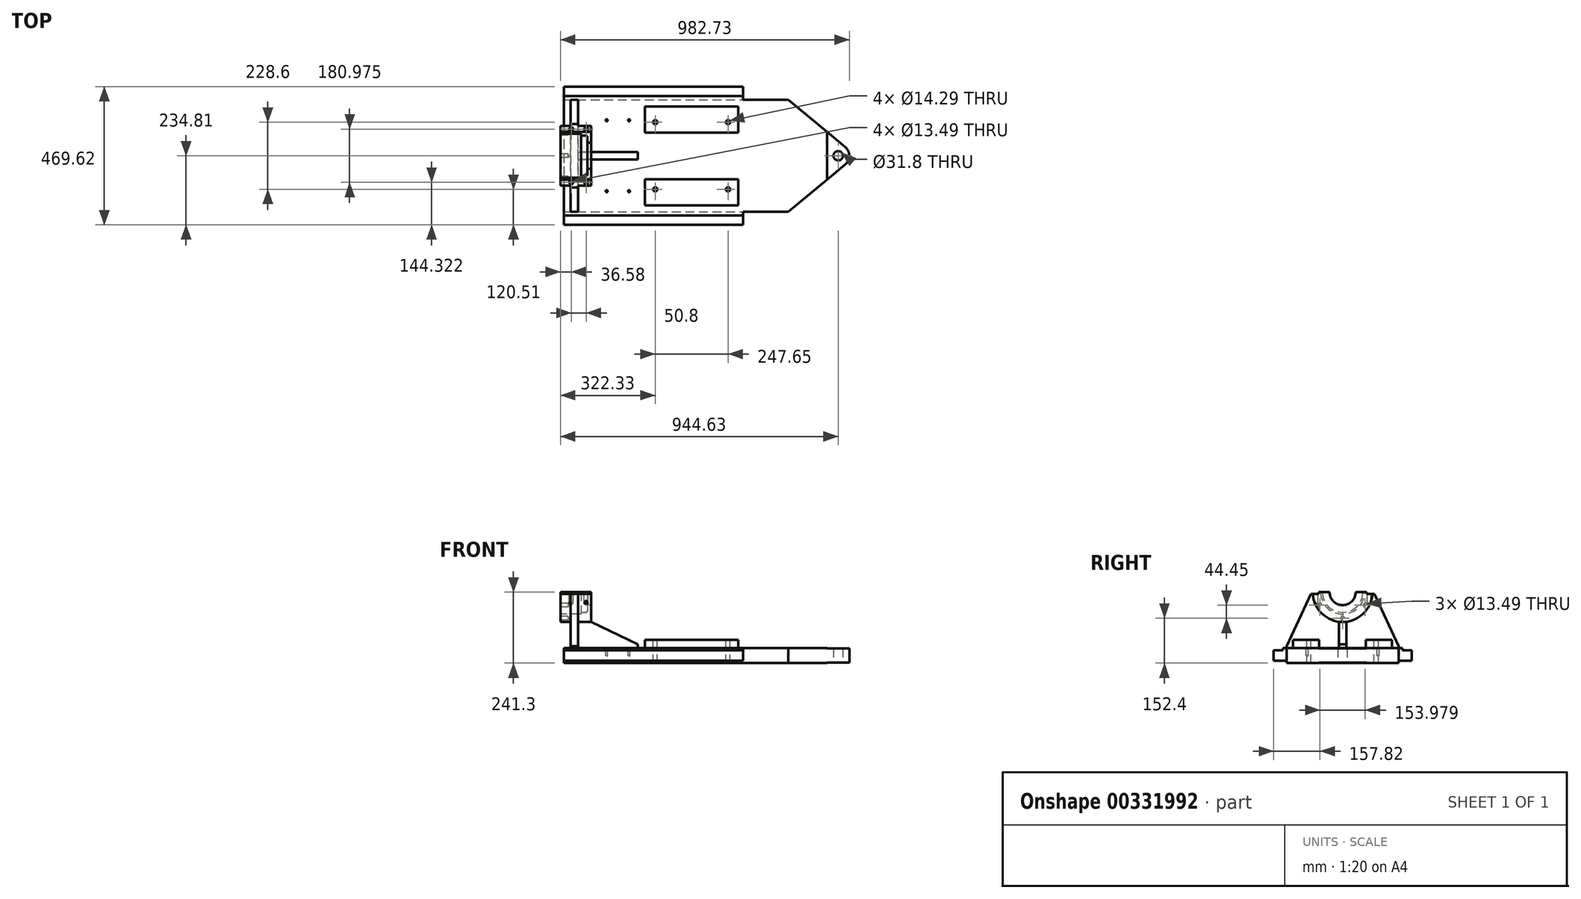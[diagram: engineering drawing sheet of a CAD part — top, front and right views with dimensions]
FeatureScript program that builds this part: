
annotation { "Feature Type Name" : "Feature", "Feature Type Description" : "" }
export const myFeature = defineFeature(function(context is Context, id is Id, definition is map)
    precondition{}
    {
        {
            var Q0;
            Q0=qCreatedBy(makeId("Top.planeOp"),FACE);
            var sketch = newSketch(context, id + "F0", { "sketchPlane" : qUnion([Q0])});
            skLineSegment(sketch, "E0.bottom", {"start": v(-304.8, 234.81) * mm, "end": v(304.8, 234.81) * mm});
            skLineSegment(sketch, "E0.top", {"start": v(-304.8, -234.81) * mm, "end": v(304.8, -234.81) * mm});
            skLineSegment(sketch, "E0.left", {"start": v(-304.8, 234.81) * mm, "end": v(-304.8, -234.81) * mm});
            skPoint(sketch, "E0.middle", {"position": v(0, 0) * mm});
            skLineSegment(sketch, "E1.0", {"start": v(666.75, 234.81) * mm, "end": v(666.75, -234.81) * mm, "construction": true});
            skLineSegment(sketch, "E2.0", {"start": v(628.65, 234.81) * mm, "end": v(628.65, -234.81) * mm, "construction": true});
            skLineSegment(sketch, "E3", {"start": v(459.57, 190.5) * mm, "end": v(653.04, 29.27) * mm});
            skLineSegment(sketch, "E4", {"start": v(459.57, -190.5) * mm, "end": v(656.3, -26.56) * mm});
            skLineSegment(sketch, "E5", {"start": v(304.8, 234.81) * mm, "end": v(304.8, 190.5) * mm});
            skLineSegment(sketch, "E6", {"start": v(-414.48, 0) * mm, "end": v(838.18, 0) * mm, "construction": true});
            skArc(sketch, "E7", {"start": v(653.04, -29.27) * mm, "mid": v(666.75, 0) * mm, "end": v(653.04, 29.27) * mm});
            skCircle(sketch, "E8", {"center": v(628.65, 0) * mm, "radius": 15.9 * mm});
            skLineSegment(sketch, "E9.0", {"start": v(-414.48, -190.5) * mm, "end": v(-304.8, -190.5) * mm});
            skLineSegment(sketch, "E10.trimOffspring", {"start": v(304.8, -190.5) * mm, "end": v(459.57, -190.5) * mm});
            skPoint(sketch, "E11.top.end.orphan", {"position": v(406.4, -234.81) * mm});
            skLineSegment(sketch, "E12.trimOffspring", {"start": v(628.65, -190.5) * mm, "end": v(838.18, -190.5) * mm});
            skLineSegment(sketch, "E13.MirrorCS", {"start": v(304.8, 190.5) * mm, "end": v(459.57, 190.5) * mm});
            skLineSegment(sketch, "E14.trimOffspring", {"start": v(304.8, -190.5) * mm, "end": v(304.8, -234.81) * mm});
            skSolve(sketch);
        }
        {
            var Q0;
            Q0 = qSketchRegion(id + "F0", true);
            extrude(context, id + "F1", {"entities" : qUnion([Q0]), "endBound" : BoundingType.SYMMETRIC, "depth" : 50.8 * mm});
        }
        {
            var Q0;
            Q0=makeQuery(id+"F1.opExtrude","CAP_FACE",FACE,{"disambiguationData":[OSD([sQuery(id+"F0.wireOp",EDGE,"E0.bottom"),sQuery(id+"F0.wireOp",EDGE,"E0.top"),sQuery(id+"F0.wireOp",EDGE,"E0.left"),sQuery(id+"F0.wireOp",EDGE,"E3"),sQuery(id+"F0.wireOp",EDGE,"E4"),sQuery(id+"F0.wireOp",EDGE,"E5"),sQuery(id+"F0.wireOp",EDGE,"E7"),sQuery(id+"F0.wireOp",EDGE,"E8"),sQuery(id+"F0.wireOp",EDGE,"E10.trimOffspring"),sQuery(id+"F0.wireOp",EDGE,"E13.MirrorCS"),sQuery(id+"F0.wireOp",EDGE,"E14.trimOffspring")])],"isStart":false});
            var sketch = newSketch(context, id + "F2", { "sketchPlane" : qUnion([Q0])});
            skCircle(sketch, "E15.0", {"center": v(628.65, 0) * mm, "radius": 15.9 * mm, "construction": true});
            skLineSegment(sketch, "E16.bottom", {"start": v(590.55, 101.6) * mm, "end": v(666.75, 101.6) * mm});
            skLineSegment(sketch, "E16.top", {"start": v(590.55, -101.6) * mm, "end": v(666.75, -101.6) * mm});
            skLineSegment(sketch, "E16.left", {"start": v(590.55, 101.6) * mm, "end": v(590.55, -101.6) * mm});
            skLineSegment(sketch, "E16.right", {"start": v(666.75, 101.6) * mm, "end": v(666.75, -101.6) * mm});
            skSolve(sketch);
        }
        {
            var Q0;
            Q0 = qSketchRegion(id + "F2", true);
            extrude(context, id + "F3", {"entities" : qUnion([Q0]), "operationType" : NewBodyOperationType.REMOVE, "oppositeDirection" : true, "depth" : 1.59 * mm});
        }
        {
            var Q0;
            Q0=makeQuery(id+"F1.opExtrude","CAP_FACE",FACE,{"disambiguationData":[OSD([sQuery(id+"F0.wireOp",EDGE,"E0.bottom"),sQuery(id+"F0.wireOp",EDGE,"E0.top"),sQuery(id+"F0.wireOp",EDGE,"E0.left"),sQuery(id+"F0.wireOp",EDGE,"E3"),sQuery(id+"F0.wireOp",EDGE,"E4"),sQuery(id+"F0.wireOp",EDGE,"E5"),sQuery(id+"F0.wireOp",EDGE,"E7"),sQuery(id+"F0.wireOp",EDGE,"E8"),sQuery(id+"F0.wireOp",EDGE,"E10.trimOffspring"),sQuery(id+"F0.wireOp",EDGE,"E13.MirrorCS"),sQuery(id+"F0.wireOp",EDGE,"E14.trimOffspring")])],"isStart":true});
            var sketch = newSketch(context, id + "F4", { "sketchPlane" : qUnion([Q0])});
            skCircle(sketch, "E17.0", {"center": v(628.65, 0) * mm, "radius": 15.9 * mm, "construction": true});
            skLineSegment(sketch, "E18.bottom", {"start": v(590.55, 101.6) * mm, "end": v(666.75, 101.6) * mm});
            skLineSegment(sketch, "E18.top", {"start": v(590.55, -101.6) * mm, "end": v(666.75, -101.6) * mm});
            skLineSegment(sketch, "E18.left", {"start": v(590.55, 101.6) * mm, "end": v(590.55, -101.6) * mm});
            skLineSegment(sketch, "E18.right", {"start": v(666.75, 101.6) * mm, "end": v(666.75, -101.6) * mm});
            skSolve(sketch);
        }
        {
            var Q0;
            Q0 = qSketchRegion(id + "F4", true);
            extrude(context, id + "F5", {"entities" : qUnion([Q0]), "operationType" : NewBodyOperationType.REMOVE, "oppositeDirection" : true, "depth" : 1.59 * mm});
        }
        {
            var Q0;
            Q0=makeQuery(id+"F1.opExtrude","CAP_FACE",FACE,{"disambiguationData":[OSD([sQuery(id+"F0.wireOp",EDGE,"E0.bottom"),sQuery(id+"F0.wireOp",EDGE,"E0.top"),sQuery(id+"F0.wireOp",EDGE,"E0.left"),sQuery(id+"F0.wireOp",EDGE,"E3"),sQuery(id+"F0.wireOp",EDGE,"E4"),sQuery(id+"F0.wireOp",EDGE,"E5"),sQuery(id+"F0.wireOp",EDGE,"E7"),sQuery(id+"F0.wireOp",EDGE,"E8"),sQuery(id+"F0.wireOp",EDGE,"E10.trimOffspring"),sQuery(id+"F0.wireOp",EDGE,"E13.MirrorCS"),sQuery(id+"F0.wireOp",EDGE,"E14.trimOffspring")])],"isStart":false});
            var sketch = newSketch(context, id + "F6", { "sketchPlane" : qUnion([Q0])});
            skLineSegment(sketch, "E19", {"start": v(-362.8, 0) * mm, "end": v(684.09, 0) * mm, "construction": true});
            skLineSegment(sketch, "E20.0", {"start": v(-362.8, -203.2) * mm, "end": v(684.09, -203.2) * mm, "construction": true});
            skLineSegment(sketch, "E21.0", {"start": v(-304.8, 234.81) * mm, "end": v(-304.8, -234.81) * mm, "construction": true});
            skLineSegment(sketch, "E22.0", {"start": v(304.8, -190.5) * mm, "end": v(304.8, -234.81) * mm, "construction": true});
            skLineSegment(sketch, "E23.bottom", {"start": v(-304.8, -234.81) * mm, "end": v(332.24, -234.81) * mm});
            skLineSegment(sketch, "E23.top", {"start": v(-304.8, -203.2) * mm, "end": v(332.24, -203.2) * mm});
            skLineSegment(sketch, "E23.left", {"start": v(-304.8, -234.81) * mm, "end": v(-304.8, -203.2) * mm});
            skLineSegment(sketch, "E23.right", {"start": v(332.24, -234.81) * mm, "end": v(332.24, -203.2) * mm});
            skLineSegment(sketch, "E24.MirrorCS", {"start": v(332.24, 234.81) * mm, "end": v(332.24, 203.2) * mm});
            skLineSegment(sketch, "E25.MirrorCS", {"start": v(-304.8, 234.81) * mm, "end": v(-304.8, 203.2) * mm});
            skLineSegment(sketch, "E26.MirrorCS", {"start": v(-304.8, 203.2) * mm, "end": v(332.24, 203.2) * mm});
            skLineSegment(sketch, "E27.MirrorCS", {"start": v(-304.8, 234.81) * mm, "end": v(332.24, 234.81) * mm});
            skLineSegment(sketch, "E28.MirrorCS", {"start": v(304.8, 190.5) * mm, "end": v(304.8, 234.81) * mm, "construction": true});
            skSolve(sketch);
        }
        {
            var Q0;
            Q0 = qSketchRegion(id + "F6", true);
            extrude(context, id + "F7", {"entities" : qUnion([Q0]), "operationType" : NewBodyOperationType.REMOVE, "oppositeDirection" : true, "depth" : 7.94 * mm});
        }
        {
            var Q0;
            Q0=makeQuery(id+"F1.opExtrude","CAP_FACE",FACE,{"disambiguationData":[OSD([sQuery(id+"F0.wireOp",EDGE,"E0.bottom"),sQuery(id+"F0.wireOp",EDGE,"E0.top"),sQuery(id+"F0.wireOp",EDGE,"E0.left"),sQuery(id+"F0.wireOp",EDGE,"E3"),sQuery(id+"F0.wireOp",EDGE,"E4"),sQuery(id+"F0.wireOp",EDGE,"E5"),sQuery(id+"F0.wireOp",EDGE,"E7"),sQuery(id+"F0.wireOp",EDGE,"E8"),sQuery(id+"F0.wireOp",EDGE,"E10.trimOffspring"),sQuery(id+"F0.wireOp",EDGE,"E13.MirrorCS"),sQuery(id+"F0.wireOp",EDGE,"E14.trimOffspring")])],"isStart":true});
            var sketch = newSketch(context, id + "F8", { "sketchPlane" : qUnion([Q0])});
            skLineSegment(sketch, "E29", {"start": v(-400.34, 0) * mm, "end": v(753.76, 0) * mm, "construction": true});
            skLineSegment(sketch, "E30.0", {"start": v(-304.8, -234.81) * mm, "end": v(-304.8, 234.81) * mm, "construction": true});
            skLineSegment(sketch, "E31.0", {"start": v(-400.34, -190.5) * mm, "end": v(753.76, -190.5) * mm, "construction": true});
            skLineSegment(sketch, "E32.bottom", {"start": v(-304.8, -190.5) * mm, "end": v(475.01, -190.5) * mm});
            skLineSegment(sketch, "E32.top", {"start": v(-304.8, -283.73) * mm, "end": v(475.01, -283.73) * mm});
            skLineSegment(sketch, "E32.left", {"start": v(-304.8, -190.5) * mm, "end": v(-304.8, -283.73) * mm});
            skLineSegment(sketch, "E32.right", {"start": v(475.01, -190.5) * mm, "end": v(475.01, -283.73) * mm});
            skLineSegment(sketch, "E33.MirrorCS", {"start": v(475.01, 190.5) * mm, "end": v(475.01, 283.73) * mm});
            skLineSegment(sketch, "E34.MirrorCS", {"start": v(-304.8, 190.5) * mm, "end": v(-304.8, 283.73) * mm});
            skLineSegment(sketch, "E35.MirrorCS", {"start": v(-304.8, 283.73) * mm, "end": v(475.01, 283.73) * mm});
            skLineSegment(sketch, "E36.MirrorCS", {"start": v(-304.8, 190.5) * mm, "end": v(475.01, 190.5) * mm});
            skSolve(sketch);
        }
        {
            var Q0;
            Q0 = qSketchRegion(id + "F8", true);
            extrude(context, id + "F9", {"entities" : qUnion([Q0]), "operationType" : NewBodyOperationType.REMOVE, "oppositeDirection" : true, "depth" : 7.94 * mm});
        }
        {
            var Q0;
            Q0=makeQuery(id+"F1.opExtrude","CAP_FACE",FACE,{"disambiguationData":[OSD([sQuery(id+"F0.wireOp",EDGE,"E0.bottom"),sQuery(id+"F0.wireOp",EDGE,"E0.top"),sQuery(id+"F0.wireOp",EDGE,"E0.left"),sQuery(id+"F0.wireOp",EDGE,"E3"),sQuery(id+"F0.wireOp",EDGE,"E4"),sQuery(id+"F0.wireOp",EDGE,"E5"),sQuery(id+"F0.wireOp",EDGE,"E7"),sQuery(id+"F0.wireOp",EDGE,"E8"),sQuery(id+"F0.wireOp",EDGE,"E10.trimOffspring"),sQuery(id+"F0.wireOp",EDGE,"E13.MirrorCS"),sQuery(id+"F0.wireOp",EDGE,"E14.trimOffspring")])],"isStart":false});
            var sketch = newSketch(context, id + "F10", { "sketchPlane" : qUnion([Q0])});
            skLineSegment(sketch, "E37", {"start": v(-417.52, 0) * mm, "end": v(724.3, 0) * mm, "construction": true});
            skLineSegment(sketch, "E38.0", {"start": v(-304.8, 203.2) * mm, "end": v(-304.8, -203.2) * mm, "construction": true});
            skLineSegment(sketch, "E39.0", {"start": v(-28.57, 203.2) * mm, "end": v(-28.57, -203.2) * mm, "construction": true});
            skLineSegment(sketch, "E40.0", {"start": v(288.93, 203.2) * mm, "end": v(288.93, -203.2) * mm, "construction": true});
            skLineSegment(sketch, "E41.0", {"start": v(-417.52, -79.38) * mm, "end": v(724.3, -79.38) * mm, "construction": true});
            skLineSegment(sketch, "E42.bottom", {"start": v(-28.57, -79.38) * mm, "end": v(288.93, -79.38) * mm});
            skLineSegment(sketch, "E42.top", {"start": v(-28.57, -168.28) * mm, "end": v(288.93, -168.28) * mm});
            skLineSegment(sketch, "E42.left", {"start": v(-28.57, -79.38) * mm, "end": v(-28.57, -168.28) * mm});
            skLineSegment(sketch, "E42.right", {"start": v(288.93, -79.38) * mm, "end": v(288.93, -168.28) * mm});
            skLineSegment(sketch, "E43.MirrorCS", {"start": v(-28.57, 168.28) * mm, "end": v(288.93, 168.28) * mm});
            skLineSegment(sketch, "E44.MirrorCS", {"start": v(288.93, 79.38) * mm, "end": v(288.93, 168.28) * mm});
            skLineSegment(sketch, "E45.MirrorCS", {"start": v(-28.57, 79.38) * mm, "end": v(-28.57, 168.28) * mm});
            skLineSegment(sketch, "E46.MirrorCS", {"start": v(-28.57, 79.38) * mm, "end": v(288.93, 79.38) * mm});
            skSolve(sketch);
        }
        {
            var Q0;
            Q0 = qSketchRegion(id + "F10", true);
            extrude(context, id + "F11", {"entities" : qUnion([Q0]), "operationType" : NewBodyOperationType.ADD, "depth" : 28.57 * mm});
        }
        {
            var Q0;
            Q0=makeQuery(id+"F11.opExtrude","CAP_FACE",FACE,{"disambiguationData":[OSD([sQuery(id+"F10.wireOp",EDGE,"E43.MirrorCS"),sQuery(id+"F10.wireOp",EDGE,"E44.MirrorCS"),sQuery(id+"F10.wireOp",EDGE,"E45.MirrorCS"),sQuery(id+"F10.wireOp",EDGE,"E46.MirrorCS")])],"isStart":false});
            var sketch = newSketch(context, id + "F12", { "sketchPlane" : qUnion([Q0])});
            skCircle(sketch, "E47.0", {"center": v(628.65, 0) * mm, "radius": 15.9 * mm, "construction": true});
            skLineSegment(sketch, "E48", {"start": v(628.65, 0) * mm, "end": v(628.65, 304) * mm, "construction": true});
            skLineSegment(sketch, "E49", {"start": v(-454.06, 0) * mm, "end": v(702.68, 0) * mm, "construction": true});
            skLineSegment(sketch, "E50.0", {"start": v(-454.06, 114.3) * mm, "end": v(702.68, 114.3) * mm, "construction": true});
            skLineSegment(sketch, "E51.0", {"start": v(254, 0) * mm, "end": v(254, 304) * mm, "construction": true});
            skLineSegment(sketch, "E52.0", {"start": v(6.35, 0) * mm, "end": v(6.35, 304) * mm, "construction": true});
            skPoint(sketch, "E53", {"position": v(6.35, 114.3) * mm});
            skPoint(sketch, "E54", {"position": v(254, 114.3) * mm});
            skPoint(sketch, "E55.MirrorP", {"position": v(254, -114.3) * mm});
            skPoint(sketch, "E56.MirrorP", {"position": v(6.35, -114.3) * mm});
            skSolve(sketch);
        }
        {
            var Q0;
            Q0=sQuery(id+"F12.wireOp",VERTEX,"E53");
            var Q1;
            Q1=sQuery(id+"F12.wireOp",VERTEX,"E54");
            var Q2;
            Q2=sQuery(id+"F12.wireOp",VERTEX,"E56.MirrorP");
            var Q3;
            Q3=sQuery(id+"F12.wireOp",VERTEX,"E55.MirrorP");
            var Q4;
            Q4=makeQuery(id+"F1.opExtrude","SWEPT_BODY",BODY,{"disambiguationData":[OSD([sQuery(id+"F0.wireOp",EDGE,"E0.bottom"),sQuery(id+"F0.wireOp",EDGE,"E0.top"),sQuery(id+"F0.wireOp",EDGE,"E0.left"),sQuery(id+"F0.wireOp",EDGE,"E3"),sQuery(id+"F0.wireOp",EDGE,"E4"),sQuery(id+"F0.wireOp",EDGE,"E5"),sQuery(id+"F0.wireOp",EDGE,"E7"),sQuery(id+"F0.wireOp",EDGE,"E8"),sQuery(id+"F0.wireOp",EDGE,"E10.trimOffspring"),sQuery(id+"F0.wireOp",EDGE,"E13.MirrorCS"),sQuery(id+"F0.wireOp",EDGE,"E14.trimOffspring")])]});
            hole(context, id + "F13", {"style" : HoleStyle.SIMPLE, "endStyle" : HoleEndStyle.THROUGH, "holeDiameter" : 14.29 * mm, "tappedDepth" : 19.53 * mm, "tapClearance" : 3, "locations" : qUnion([Q0, Q1, Q2, Q3]), "scope" : qUnion([Q4])});
        }
        {
            var Q0;
            Q0=makeQuery(id+"F1.opExtrude","CAP_FACE",FACE,{"disambiguationData":[OSD([sQuery(id+"F0.wireOp",EDGE,"E0.bottom"),sQuery(id+"F0.wireOp",EDGE,"E0.top"),sQuery(id+"F0.wireOp",EDGE,"E0.left"),sQuery(id+"F0.wireOp",EDGE,"E3"),sQuery(id+"F0.wireOp",EDGE,"E4"),sQuery(id+"F0.wireOp",EDGE,"E5"),sQuery(id+"F0.wireOp",EDGE,"E7"),sQuery(id+"F0.wireOp",EDGE,"E8"),sQuery(id+"F0.wireOp",EDGE,"E10.trimOffspring"),sQuery(id+"F0.wireOp",EDGE,"E13.MirrorCS"),sQuery(id+"F0.wireOp",EDGE,"E14.trimOffspring")])],"isStart":false});
            var sketch = newSketch(context, id + "F14", { "sketchPlane" : qUnion([Q0])});
            skLineSegment(sketch, "E57.0", {"start": v(-304.8, 203.2) * mm, "end": v(-304.8, -203.2) * mm, "construction": true});
            skLineSegment(sketch, "E58.0", {"start": v(-280.99, 203.2) * mm, "end": v(-280.99, -203.2) * mm, "construction": true});
            skLineSegment(sketch, "E59", {"start": v(-408.3, 0) * mm, "end": v(198.31, 0) * mm, "construction": true});
            skLineSegment(sketch, "E60.0", {"start": v(-408.3, -190.5) * mm, "end": v(198.31, -190.5) * mm, "construction": true});
            skLineSegment(sketch, "E61.bottom", {"start": v(-280.99, -190.5) * mm, "end": v(-255.59, -190.5) * mm});
            skLineSegment(sketch, "E61.top", {"start": v(-280.99, 190.5) * mm, "end": v(-255.59, 190.5) * mm});
            skLineSegment(sketch, "E61.left", {"start": v(-280.99, -190.5) * mm, "end": v(-280.99, 190.5) * mm});
            skLineSegment(sketch, "E61.right", {"start": v(-255.59, -190.5) * mm, "end": v(-255.59, 190.5) * mm});
            skSolve(sketch);
        }
        {
            var Q0;
            Q0 = qSketchRegion(id + "F14", true);
            extrude(context, id + "F15", {"entities" : qUnion([Q0]), "operationType" : NewBodyOperationType.ADD, "depth" : 190.5 * mm});
        }
        {
            var Q0;
            Q0=makeQuery(id+"F1.opExtrude","SWEPT_FACE",FACE,{"disambiguationData":[OSD([sQuery(id+"F0.wireOp",EDGE,"E0.left")])]});
            cPlane(context, id + "F16", {"entities" : qUnion([Q0]), "cplaneType" : CPlaneType.OFFSET, "offset" : 11.18 * mm, "width" : 152.4 * mm, "height" : 152.4 * mm});
        }
        {
            var Q0;
            Q0=qCreatedBy(id+"F16.planeOp",FACE);
            var sketch = newSketch(context, id + "F17", { "sketchPlane" : qUnion([Q0])});
            skLineSegment(sketch, "E62.0", {"start": v(190.5, 215.9) * mm, "end": v(-190.5, 215.9) * mm, "construction": true});
            skLineSegment(sketch, "E63", {"start": v(0, 334.76) * mm, "end": v(0, -159.92) * mm, "construction": true});
            skCircle(sketch, "E64", {"center": v(0, 215.9) * mm, "radius": 101.6 * mm});
            skSolve(sketch);
        }
        {
            var Q0;
            Q0 = qSketchRegion(id + "F17", true);
            extrude(context, id + "F18", {"entities" : qUnion([Q0]), "operationType" : NewBodyOperationType.ADD, "oppositeDirection" : true, "depth" : 104.77 * mm});
        }
        {
            var Q0;
            Q0=makeQuery(id+"F15.opExtrude","SWEPT_FACE",FACE,{"disambiguationData":[OSD([sQuery(id+"F14.wireOp",EDGE,"E61.left")])]});
            var sketch = newSketch(context, id + "F19", { "sketchPlane" : qUnion([Q0])});
            skCircle(sketch, "E65.0", {"center": v(0, 215.9) * mm, "radius": 101.6 * mm, "construction": true});
            skLineSegment(sketch, "E66.0", {"start": v(-203.2, 31.75) * mm, "end": v(203.2, 31.75) * mm, "construction": true});
            skLineSegment(sketch, "E67.0", {"start": v(-190.5, 215.9) * mm, "end": v(-190.5, 25.4) * mm, "construction": true});
            skLineSegment(sketch, "E68", {"start": v(-190.5, 31.75) * mm, "end": v(-107.95, 209.55) * mm});
            skLineSegment(sketch, "E69", {"start": v(-107.95, 209.55) * mm, "end": v(-80.96, 209.55) * mm});
            skLineSegment(sketch, "E70", {"start": v(-80.96, 209.55) * mm, "end": v(-80.96, 215.9) * mm});
            skLineSegment(sketch, "E71", {"start": v(-80.96, 215.9) * mm, "end": v(0, 215.9) * mm});
            skLineSegment(sketch, "E72", {"start": v(0, 356.38) * mm, "end": v(0, -105.82) * mm, "construction": true});
            skLineSegment(sketch, "E73.MirrorCS", {"start": v(80.96, 209.55) * mm, "end": v(80.96, 215.9) * mm});
            skLineSegment(sketch, "E74.MirrorCS", {"start": v(80.96, 215.9) * mm, "end": v(0, 215.9) * mm});
            skLineSegment(sketch, "E75.MirrorCS", {"start": v(190.5, 31.75) * mm, "end": v(107.95, 209.55) * mm});
            skLineSegment(sketch, "E76.MirrorCS", {"start": v(190.5, 215.9) * mm, "end": v(190.5, 25.4) * mm, "construction": true});
            skLineSegment(sketch, "E77.MirrorCS", {"start": v(107.95, 209.55) * mm, "end": v(80.96, 209.55) * mm});
            skLineSegment(sketch, "E78", {"start": v(-190.5, 31.75) * mm, "end": v(-190.5, 348.54) * mm});
            skLineSegment(sketch, "E79", {"start": v(-190.5, 348.54) * mm, "end": v(190.5, 348.54) * mm});
            skLineSegment(sketch, "E80", {"start": v(190.5, 348.54) * mm, "end": v(190.5, 31.75) * mm});
            skSolve(sketch);
        }
        {
            var Q0;
            Q0 = qSketchRegion(id + "F19", true);
            extrude(context, id + "F20", {"entities" : qUnion([Q0]), "operationType" : NewBodyOperationType.REMOVE, "endBound" : BoundingType.SYMMETRIC, "oppositeDirection" : true, "depth" : 152.4 * mm});
        }
        {
            var Q0;
            Q0=makeQuery(id+"F18.opExtrude","CAP_FACE",FACE,{"disambiguationData":[OSD([sQuery(id+"F17.wireOp",EDGE,"E64")])],"isStart":true});
            var sketch = newSketch(context, id + "F21", { "sketchPlane" : qUnion([Q0])});
            skCircle(sketch, "E81", {"center": v(0, 215.9) * mm, "radius": 44.45 * mm});
            skSolve(sketch);
        }
        {
            var Q0;
            Q0 = qSketchRegion(id + "F21", true);
            extrude(context, id + "F22", {"entities" : qUnion([Q0]), "operationType" : NewBodyOperationType.REMOVE, "endBound" : BoundingType.THROUGH_ALL, "oppositeDirection" : true, "depth" : 25.4 * mm});
        }
        {
            var Q0;
            Q0=makeQuery(id+"F18.opExtrude","CAP_FACE",FACE,{"disambiguationData":[OSD([sQuery(id+"F17.wireOp",EDGE,"E64")])],"isStart":true});
            var sketch = newSketch(context, id + "F23", { "sketchPlane" : qUnion([Q0])});
            skArc(sketch, "E82.0", {"start": v(-44.45, 215.9) * mm, "mid": v(0, 171.45) * mm, "end": v(44.45, 215.9) * mm, "construction": true});
            skCircle(sketch, "E83", {"center": v(0, 215.9) * mm, "radius": 69.09 * mm});
            skSolve(sketch);
        }
        {
            var Q0;
            Q0 = qSketchRegion(id + "F23", true);
            extrude(context, id + "F24", {"entities" : qUnion([Q0]), "operationType" : NewBodyOperationType.REMOVE, "oppositeDirection" : true, "depth" : 92.07 * mm});
        }
        {
            var Q0;
            Q0=makeQuery(id+"F18.opExtrude","CAP_FACE",FACE,{"disambiguationData":[OSD([sQuery(id+"F17.wireOp",EDGE,"E64")])],"isStart":true});
            var sketch = newSketch(context, id + "F25", { "sketchPlane" : qUnion([Q0])});
            skArc(sketch, "E84.0", {"start": v(44.45, 215.9) * mm, "mid": v(0, 171.45) * mm, "end": v(-44.45, 215.9) * mm, "construction": true});
            skCircle(sketch, "E85", {"center": v(0, 215.9) * mm, "radius": 74.93 * mm});
            skSolve(sketch);
        }
        {
            var Q0;
            Q0 = qSketchRegion(id + "F25", true);
            extrude(context, id + "F26", {"entities" : qUnion([Q0]), "operationType" : NewBodyOperationType.REMOVE, "oppositeDirection" : true, "depth" : 69.85 * mm});
        }
        {
            var Q0;
            Q0=makeQuery(id+"F20.boolean.opBoolean","COPY",FACE,{"derivedFrom":makeQuery(id+"F20.opExtrude","SWEPT_FACE",FACE,{"disambiguationData":[OSD([sQuery(id+"F19.wireOp",EDGE,"E69")])]})});
            var sketch = newSketch(context, id + "F27", { "sketchPlane" : qUnion([Q0])});
            skLineSegment(sketch, "E86", {"start": v(-429.52, 0) * mm, "end": v(-135.24, 0) * mm, "construction": true});
            skLineSegment(sketch, "E87.0", {"start": v(-315.98, 101.4) * mm, "end": v(-315.98, 80.96) * mm, "construction": true});
            skLineSegment(sketch, "E88.0", {"start": v(-429.52, 90.49) * mm, "end": v(-135.24, 90.49) * mm, "construction": true});
            skLineSegment(sketch, "E89.0", {"start": v(-279.4, 101.4) * mm, "end": v(-279.4, 80.96) * mm, "construction": true});
            skLineSegment(sketch, "E90.0", {"start": v(-228.6, 101.4) * mm, "end": v(-228.6, 80.96) * mm, "construction": true});
            skPoint(sketch, "E91", {"position": v(-279.4, 90.49) * mm});
            skPoint(sketch, "E92", {"position": v(-228.6, 90.49) * mm});
            skPoint(sketch, "E93.MirrorP", {"position": v(-279.4, -90.49) * mm});
            skPoint(sketch, "E94.MirrorP", {"position": v(-228.6, -90.49) * mm});
            skSolve(sketch);
        }
        {
            var Q0;
            Q0=sQuery(id+"F27.wireOp",VERTEX,"E91");
            var Q1;
            Q1=sQuery(id+"F27.wireOp",VERTEX,"E92");
            var Q2;
            Q2=sQuery(id+"F27.wireOp",VERTEX,"E93.MirrorP");
            var Q3;
            Q3=sQuery(id+"F27.wireOp",VERTEX,"E94.MirrorP");
            var Q4;
            Q4=makeQuery(id+"F1.opExtrude","SWEPT_BODY",BODY,{"disambiguationData":[OSD([sQuery(id+"F0.wireOp",EDGE,"E0.bottom"),sQuery(id+"F0.wireOp",EDGE,"E0.top"),sQuery(id+"F0.wireOp",EDGE,"E0.left"),sQuery(id+"F0.wireOp",EDGE,"E3"),sQuery(id+"F0.wireOp",EDGE,"E4"),sQuery(id+"F0.wireOp",EDGE,"E5"),sQuery(id+"F0.wireOp",EDGE,"E7"),sQuery(id+"F0.wireOp",EDGE,"E8"),sQuery(id+"F0.wireOp",EDGE,"E10.trimOffspring"),sQuery(id+"F0.wireOp",EDGE,"E13.MirrorCS"),sQuery(id+"F0.wireOp",EDGE,"E14.trimOffspring")])]});
            hole(context, id + "F28", {"style" : HoleStyle.SIMPLE, "endStyle" : HoleEndStyle.BLIND, "standardTappedOrClearance" : lookupTablePath({ "standard" : "ANSI", "fit" : "Normal (ASME)", "size" : "1/2", "type" : "Clearance" }), "standardBlindInLast" : lookupTablePath({ "fit" : "Free", "standard" : "ANSI", "size" : "1/2", "type" : "Clearance" }), "holeDiameter" : 13.5 * mm, "holeDepth" : 31.75 * mm, "tappedDepth" : 19.53 * mm, "tapClearance" : 3, "locations" : qUnion([Q0, Q1, Q2, Q3]), "scope" : qUnion([Q4])});
        }
        {
            var Q0;
            Q0=qCreatedBy(makeId("Front.planeOp"),FACE);
            var sketch = newSketch(context, id + "F29", { "sketchPlane" : qUnion([Q0])});
            skLineSegment(sketch, "E95", {"start": v(-211.2, 114.3) * mm, "end": v(-255.59, 114.3) * mm});
            skLineSegment(sketch, "E96.0", {"start": v(-304.8, 25.4) * mm, "end": v(304.8, 25.4) * mm});
            skLineSegment(sketch, "E97.0", {"start": v(-255.59, 31.75) * mm, "end": v(-255.59, 209.55) * mm});
            skLineSegment(sketch, "E98.0", {"start": v(-255.59, 31.75) * mm, "end": v(-255.59, 25.4) * mm});
            skLineSegment(sketch, "E99.0", {"start": v(-52.39, 25.4) * mm, "end": v(-52.39, 209.55) * mm});
            skLineSegment(sketch, "E100.0", {"start": v(-304.8, 38.1) * mm, "end": v(304.8, 38.1) * mm, "construction": true});
            skLineSegment(sketch, "E101", {"start": v(-211.2, 114.3) * mm, "end": v(-52.39, 38.1) * mm});
            skSolve(sketch);
        }
        {
            var Q0;
            Q0 = qSketchRegion(id + "F29", true);
            extrude(context, id + "F30", {"entities" : qUnion([Q0]), "endBound" : BoundingType.SYMMETRIC, "depth" : 25.4 * mm});
        }
        {
            var Q0;
            Q0=makeQuery(id+"F1.opExtrude","CAP_FACE",FACE,{"disambiguationData":[OSD([sQuery(id+"F0.wireOp",EDGE,"E0.bottom"),sQuery(id+"F0.wireOp",EDGE,"E0.top"),sQuery(id+"F0.wireOp",EDGE,"E0.left"),sQuery(id+"F0.wireOp",EDGE,"E3"),sQuery(id+"F0.wireOp",EDGE,"E4"),sQuery(id+"F0.wireOp",EDGE,"E5"),sQuery(id+"F0.wireOp",EDGE,"E7"),sQuery(id+"F0.wireOp",EDGE,"E8"),sQuery(id+"F0.wireOp",EDGE,"E10.trimOffspring"),sQuery(id+"F0.wireOp",EDGE,"E13.MirrorCS"),sQuery(id+"F0.wireOp",EDGE,"E14.trimOffspring")])],"isStart":false});
            var sketch = newSketch(context, id + "F31", { "sketchPlane" : qUnion([Q0])});
            skCircle(sketch, "E102.0", {"center": v(6.35, 114.3) * mm, "radius": 7.14 * mm, "construction": true});
            skLineSegment(sketch, "E103", {"start": v(6.35, 114.3) * mm, "end": v(6.35, -303.64) * mm, "construction": true});
            skLineSegment(sketch, "E104", {"start": v(-451.94, 0) * mm, "end": v(697.13, 0) * mm, "construction": true});
            skLineSegment(sketch, "E105.0", {"start": v(-82.55, 114.3) * mm, "end": v(-82.55, -303.64) * mm, "construction": true});
            skLineSegment(sketch, "E106.0", {"start": v(-158.75, 114.3) * mm, "end": v(-158.75, -303.64) * mm, "construction": true});
            skLineSegment(sketch, "E107.0", {"start": v(-451.94, -120.65) * mm, "end": v(697.13, -120.65) * mm, "construction": true});
            skPoint(sketch, "E108", {"position": v(-158.75, -120.65) * mm});
            skPoint(sketch, "E109", {"position": v(-82.55, -120.65) * mm});
            skPoint(sketch, "E110.MirrorP", {"position": v(-158.75, 120.65) * mm});
            skPoint(sketch, "E111.MirrorP", {"position": v(-82.55, 120.65) * mm});
            skSolve(sketch);
        }
        {
            var Q0;
            Q0=sQuery(id+"F31.wireOp",VERTEX,"E111.MirrorP");
            var Q1;
            Q1=sQuery(id+"F31.wireOp",VERTEX,"E110.MirrorP");
            var Q2;
            Q2=sQuery(id+"F31.wireOp",VERTEX,"E109");
            var Q3;
            Q3=sQuery(id+"F31.wireOp",VERTEX,"E108");
            var Q4;
            Q4=makeQuery(id+"F1.opExtrude","SWEPT_BODY",BODY,{"disambiguationData":[OSD([sQuery(id+"F0.wireOp",EDGE,"E0.bottom"),sQuery(id+"F0.wireOp",EDGE,"E0.top"),sQuery(id+"F0.wireOp",EDGE,"E0.left"),sQuery(id+"F0.wireOp",EDGE,"E3"),sQuery(id+"F0.wireOp",EDGE,"E4"),sQuery(id+"F0.wireOp",EDGE,"E5"),sQuery(id+"F0.wireOp",EDGE,"E7"),sQuery(id+"F0.wireOp",EDGE,"E8"),sQuery(id+"F0.wireOp",EDGE,"E10.trimOffspring"),sQuery(id+"F0.wireOp",EDGE,"E13.MirrorCS"),sQuery(id+"F0.wireOp",EDGE,"E14.trimOffspring")])]});
            hole(context, id + "F32", {"style" : HoleStyle.SIMPLE, "endStyle" : HoleEndStyle.BLIND, "standardTappedOrClearance" : lookupTablePath({ "standard" : "ANSI", "fit" : "Normal (ASME)", "size" : "1/4", "type" : "Clearance" }), "standardBlindInLast" : lookupTablePath({ "fit" : "Free", "standard" : "ANSI", "size" : "1/4", "type" : "Clearance" }), "holeDiameter" : 6.76 * mm, "holeDepth" : 25.4 * mm, "tappedDepth" : 19.53 * mm, "tapClearance" : 3, "locations" : qUnion([Q0, Q1, Q2, Q3]), "scope" : qUnion([Q4])});
        }
        {
            var Q0;
            Q0=makeQuery(id+"F18.opExtrude","CAP_FACE",FACE,{"disambiguationData":[OSD([sQuery(id+"F17.wireOp",EDGE,"E64")])],"isStart":true});
            var sketch = newSketch(context, id + "F33", { "sketchPlane" : qUnion([Q0])});
            skArc(sketch, "E112.0", {"start": v(44.45, 215.9) * mm, "mid": v(0, 171.45) * mm, "end": v(-44.45, 215.9) * mm, "construction": true});
            skCircle(sketch, "E113", {"center": v(0, 215.9) * mm, "radius": 88.9 * mm, "construction": true});
            skLineSegment(sketch, "E114", {"start": v(0, 215.9) * mm, "end": v(0, -126.02) * mm, "construction": true});
            skLineSegment(sketch, "E115", {"start": v(0, 215.9) * mm, "end": v(325.66, 27.88) * mm, "construction": true});
            skPoint(sketch, "E116", {"position": v(0, 127) * mm});
            skPoint(sketch, "E117", {"position": v(76.99, 171.45) * mm});
            skPoint(sketch, "E118.MirrorP", {"position": v(-76.99, 171.45) * mm});
            skSolve(sketch);
        }
        {
            var Q0;
            Q0=sQuery(id+"F33.wireOp",VERTEX,"E118.MirrorP");
            var Q1;
            Q1=sQuery(id+"F33.wireOp",VERTEX,"E116");
            var Q2;
            Q2=sQuery(id+"F33.wireOp",VERTEX,"E117");
            var Q3;
            Q3=makeQuery(id+"F1.opExtrude","SWEPT_BODY",BODY,{"disambiguationData":[OSD([sQuery(id+"F0.wireOp",EDGE,"E0.bottom"),sQuery(id+"F0.wireOp",EDGE,"E0.top"),sQuery(id+"F0.wireOp",EDGE,"E0.left"),sQuery(id+"F0.wireOp",EDGE,"E3"),sQuery(id+"F0.wireOp",EDGE,"E4"),sQuery(id+"F0.wireOp",EDGE,"E5"),sQuery(id+"F0.wireOp",EDGE,"E7"),sQuery(id+"F0.wireOp",EDGE,"E8"),sQuery(id+"F0.wireOp",EDGE,"E10.trimOffspring"),sQuery(id+"F0.wireOp",EDGE,"E13.MirrorCS"),sQuery(id+"F0.wireOp",EDGE,"E14.trimOffspring")])]});
            hole(context, id + "F34", {"style" : HoleStyle.SIMPLE, "endStyle" : HoleEndStyle.BLIND, "standardTappedOrClearance" : lookupTablePath({ "standard" : "ANSI", "fit" : "Normal (ASME)", "size" : "1/2", "type" : "Clearance" }), "standardBlindInLast" : lookupTablePath({ "fit" : "Free", "standard" : "ANSI", "size" : "1/2", "type" : "Clearance" }), "holeDiameter" : 13.5 * mm, "holeDepth" : 25.4 * mm, "tappedDepth" : 19.53 * mm, "tapClearance" : 3, "locations" : qUnion([Q0, Q1, Q2]), "scope" : qUnion([Q3])});
        }
        {
            var Q0;
            Q0=makeQuery(id+"F24.boolean.opBoolean","COPY",EDGE,{"derivedFrom":makeQuery(id+"F24.opExtrude","CAP_EDGE",EDGE,{"disambiguationData":[OSD([sQuery(id+"F23.wireOp",EDGE,"E83")])],"isStart":false})});
            fillet(context, id + "F35", {"entities" : qUnion([Q0]), "radius" : 6.35 * mm, "tangentPropagation" : true, "allowEdgeOverflow" : false});
        }
        {
            var Q0;
            Q0=makeQuery(id+"F26.boolean.opBoolean","COPY",EDGE,{"derivedFrom":makeQuery(id+"F26.opExtrude","CAP_EDGE",EDGE,{"disambiguationData":[OSD([sQuery(id+"F25.wireOp",EDGE,"E85")])],"isStart":false})});
            fillet(context, id + "F36", {"entities" : qUnion([Q0]), "radius" : 1.59 * mm, "tangentPropagation" : true, "allowEdgeOverflow" : false});
        }
    });
